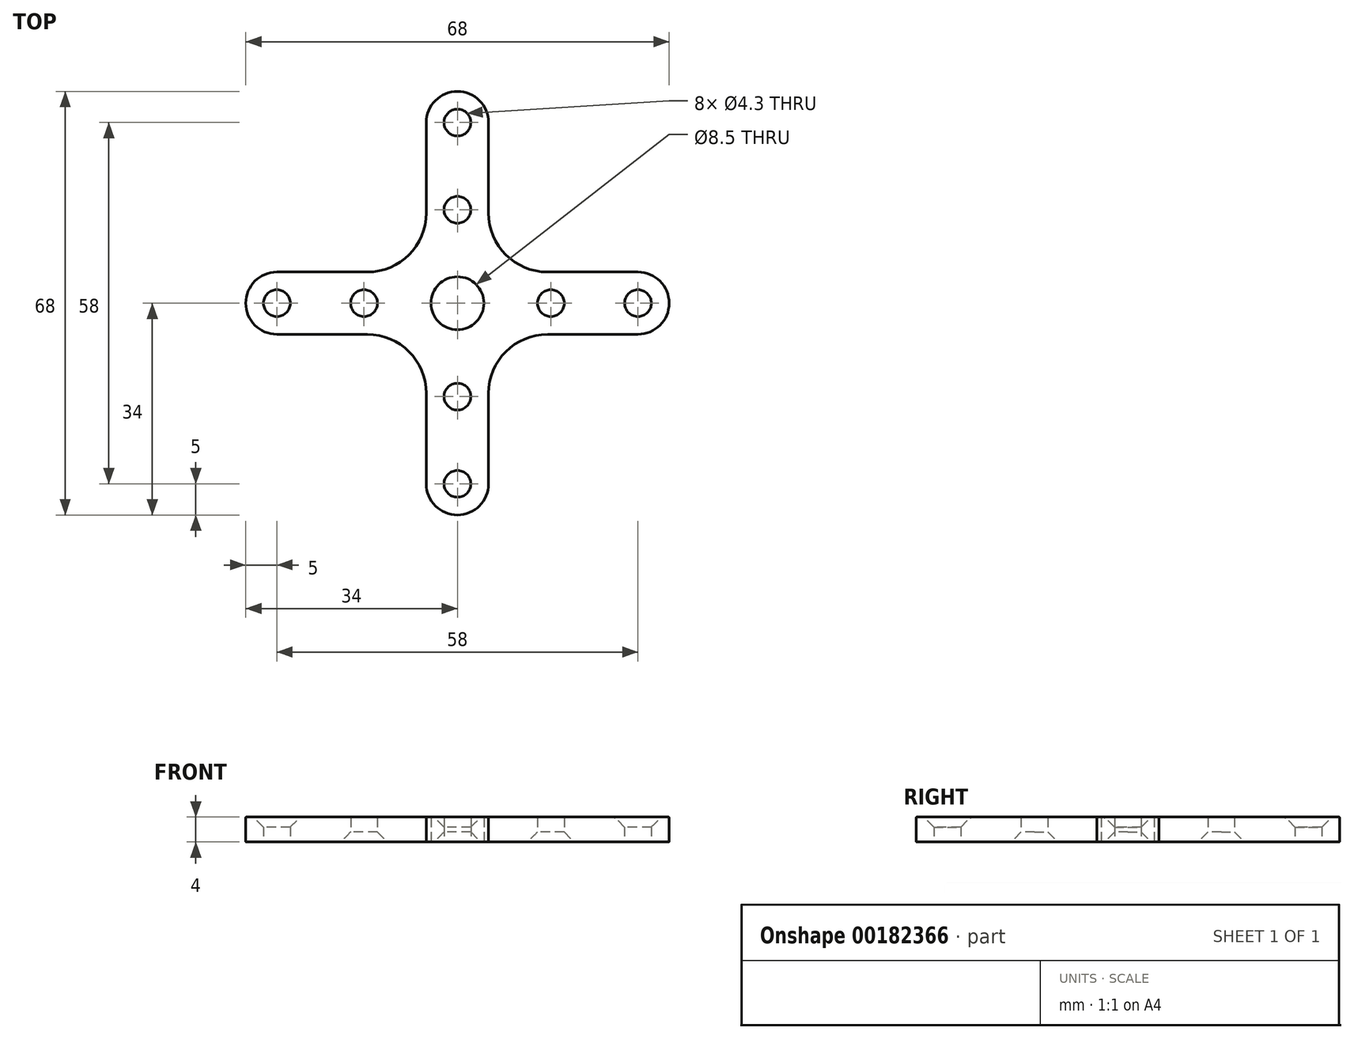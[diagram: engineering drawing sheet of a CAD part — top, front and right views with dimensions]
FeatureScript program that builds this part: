
annotation { "Feature Type Name" : "Feature", "Feature Type Description" : "" }
export const myFeature = defineFeature(function(context is Context, id is Id, definition is map)
    precondition{}
    {
        {
            var Q0;
            Q0=qCreatedBy(makeId("Top.planeOp"),FACE);
            var sketch = newSketch(context, id + "F0", { "sketchPlane" : qUnion([Q0])});
            skCircle(sketch, "E0", {"center": v(0, 0) * mm, "radius": 34 * mm, "construction": true});
            skCircle(sketch, "E1", {"center": v(0, 0) * mm, "radius": 29 * mm, "construction": true});
            skLineSegment(sketch, "E2", {"start": v(0, -42.55) * mm, "end": v(0, 44.51) * mm, "construction": true});
            skLineSegment(sketch, "E3", {"start": v(-47.28, 0) * mm, "end": v(50.22, 0) * mm, "construction": true});
            skCircle(sketch, "E4", {"center": v(0, 0) * mm, "radius": 11 * mm, "construction": true});
            skArc(sketch, "E5", {"start": v(5, 29) * mm, "mid": v(0, 34) * mm, "end": v(-5, 29) * mm});
            skArc(sketch, "E6", {"start": v(-29, 5) * mm, "mid": v(-34, 0) * mm, "end": v(-29, -5) * mm});
            skArc(sketch, "E7", {"start": v(29, -5) * mm, "mid": v(34, 0) * mm, "end": v(29, 5) * mm});
            skArc(sketch, "E8", {"start": v(-5, -29) * mm, "mid": v(0, -34) * mm, "end": v(5, -29) * mm});
            skArc(sketch, "E9", {"start": v(14.49, -5) * mm, "mid": v(7.78, -7.78) * mm, "end": v(5, -14.49) * mm});
            skArc(sketch, "E10", {"start": v(5, 14.49) * mm, "mid": v(7.78, 7.78) * mm, "end": v(14.49, 5) * mm});
            skArc(sketch, "E11", {"start": v(-14.49, 5) * mm, "mid": v(-7.78, 7.78) * mm, "end": v(-5, 14.49) * mm});
            skArc(sketch, "E12", {"start": v(-5, -14.49) * mm, "mid": v(-7.78, -7.78) * mm, "end": v(-14.49, -5) * mm});
            skCircle(sketch, "E13", {"center": v(0, 29) * mm, "radius": 2.15 * mm});
            skCircle(sketch, "E14", {"center": v(29, 0) * mm, "radius": 2.15 * mm});
            skCircle(sketch, "E15", {"center": v(0, -29) * mm, "radius": 2.15 * mm});
            skCircle(sketch, "E16", {"center": v(-29, 0) * mm, "radius": 2.15 * mm});
            skLineSegment(sketch, "E17.trimOffspring", {"start": v(-5, 14.49) * mm, "end": v(-5, 29) * mm});
            skLineSegment(sketch, "E18.trimOffspring", {"start": v(5, 14.49) * mm, "end": v(5, 29) * mm});
            skLineSegment(sketch, "E19.trimOffspring", {"start": v(14.49, 5) * mm, "end": v(29, 5) * mm});
            skLineSegment(sketch, "E20.trimOffspring", {"start": v(14.49, -5) * mm, "end": v(29, -5) * mm});
            skLineSegment(sketch, "E21.trimOffspring", {"start": v(-29, 5) * mm, "end": v(-14.49, 5) * mm});
            skLineSegment(sketch, "E22.trimOffspring", {"start": v(-29, -5) * mm, "end": v(-14.49, -5) * mm});
            skLineSegment(sketch, "E23.trimOffspring", {"start": v(-5, -29) * mm, "end": v(-5, -14.49) * mm});
            skLineSegment(sketch, "E24.trimOffspring", {"start": v(5, -29) * mm, "end": v(5, -14.49) * mm});
            skCircle(sketch, "E25", {"center": v(0, 0) * mm, "radius": 4.25 * mm});
            skCircle(sketch, "E26", {"center": v(0, 0) * mm, "radius": 15 * mm, "construction": true});
            skCircle(sketch, "E27", {"center": v(0, 15) * mm, "radius": 2.15 * mm});
            skCircle(sketch, "E28", {"center": v(-15, 0) * mm, "radius": 2.15 * mm});
            skCircle(sketch, "E29", {"center": v(0, -15) * mm, "radius": 2.15 * mm});
            skCircle(sketch, "E30", {"center": v(15, 0) * mm, "radius": 2.15 * mm});
            skSolve(sketch);
        }
        {
            var Q0;
            Q0 = qSketchRegion(id + "F0", true);
            extrude(context, id + "F1", {"entities" : qUnion([Q0]), "depth" : 4 * mm});
        }
        {
            var Q0;
            Q0=makeQuery(id+"F1.opExtrude","CAP_EDGE",EDGE,{"disambiguationData":[OSD([sQuery(id+"F0.wireOp",EDGE,"E13")])],"isStart":false});
            var Q1;
            Q1=makeQuery(id+"F1.opExtrude","CAP_EDGE",EDGE,{"disambiguationData":[OSD([sQuery(id+"F0.wireOp",EDGE,"E14")])],"isStart":false});
            var Q2;
            Q2=makeQuery(id+"F1.opExtrude","CAP_EDGE",EDGE,{"disambiguationData":[OSD([sQuery(id+"F0.wireOp",EDGE,"E15")])],"isStart":false});
            var Q3;
            Q3=makeQuery(id+"F1.opExtrude","CAP_EDGE",EDGE,{"disambiguationData":[OSD([sQuery(id+"F0.wireOp",EDGE,"E16")])],"isStart":false});
            chamfer(context, id + "F2", {"entities" : qUnion([Q0, Q1, Q2, Q3]), "width" : 1.6 * mm, "tangentPropagation" : true});
        }
        {
            var Q0;
            Q0=makeQuery(id+"F1.opExtrude","CAP_EDGE",EDGE,{"disambiguationData":[OSD([sQuery(id+"F0.wireOp",EDGE,"E29")])],"isStart":true});
            var Q1;
            Q1=makeQuery(id+"F1.opExtrude","CAP_EDGE",EDGE,{"disambiguationData":[OSD([sQuery(id+"F0.wireOp",EDGE,"E28")])],"isStart":true});
            var Q2;
            Q2=makeQuery(id+"F1.opExtrude","CAP_EDGE",EDGE,{"disambiguationData":[OSD([sQuery(id+"F0.wireOp",EDGE,"E27")])],"isStart":true});
            var Q3;
            Q3=makeQuery(id+"F1.opExtrude","CAP_EDGE",EDGE,{"disambiguationData":[OSD([sQuery(id+"F0.wireOp",EDGE,"E30")])],"isStart":true});
            chamfer(context, id + "F3", {"entities" : qUnion([Q0, Q1, Q2, Q3]), "width" : 1.6 * mm, "tangentPropagation" : true});
        }
        {
            var Q0;
            Q0=makeQuery(id+"F1.opExtrude","CAP_FACE",FACE,{"disambiguationData":[OSD([sQuery(id+"F0.wireOp",EDGE,"E5"),sQuery(id+"F0.wireOp",EDGE,"E6"),sQuery(id+"F0.wireOp",EDGE,"E7"),sQuery(id+"F0.wireOp",EDGE,"E8"),sQuery(id+"F0.wireOp",EDGE,"E9"),sQuery(id+"F0.wireOp",EDGE,"E10"),sQuery(id+"F0.wireOp",EDGE,"E11"),sQuery(id+"F0.wireOp",EDGE,"E12"),sQuery(id+"F0.wireOp",EDGE,"E13"),sQuery(id+"F0.wireOp",EDGE,"E14"),sQuery(id+"F0.wireOp",EDGE,"E15"),sQuery(id+"F0.wireOp",EDGE,"E16"),sQuery(id+"F0.wireOp",EDGE,"E17.trimOffspring"),sQuery(id+"F0.wireOp",EDGE,"E18.trimOffspring"),sQuery(id+"F0.wireOp",EDGE,"E19.trimOffspring"),sQuery(id+"F0.wireOp",EDGE,"E20.trimOffspring"),sQuery(id+"F0.wireOp",EDGE,"E21.trimOffspring"),sQuery(id+"F0.wireOp",EDGE,"E22.trimOffspring"),sQuery(id+"F0.wireOp",EDGE,"E23.trimOffspring"),sQuery(id+"F0.wireOp",EDGE,"E24.trimOffspring"),sQuery(id+"F0.wireOp",EDGE,"E25"),sQuery(id+"F0.wireOp",EDGE,"E27"),sQuery(id+"F0.wireOp",EDGE,"E28"),sQuery(id+"F0.wireOp",EDGE,"E29"),sQuery(id+"F0.wireOp",EDGE,"E30")])],"isStart":false});
            fillet(context, id + "F4", {"entities" : qUnion([Q0]), "radius" : 0.1 * mm, "tangentPropagation" : true, "allowEdgeOverflow" : false});
        }
        {
            var Q0;
            Q0=makeQuery(id+"F1.opExtrude","CAP_FACE",FACE,{"disambiguationData":[OSD([sQuery(id+"F0.wireOp",EDGE,"E5"),sQuery(id+"F0.wireOp",EDGE,"E6"),sQuery(id+"F0.wireOp",EDGE,"E7"),sQuery(id+"F0.wireOp",EDGE,"E8"),sQuery(id+"F0.wireOp",EDGE,"E9"),sQuery(id+"F0.wireOp",EDGE,"E10"),sQuery(id+"F0.wireOp",EDGE,"E11"),sQuery(id+"F0.wireOp",EDGE,"E12"),sQuery(id+"F0.wireOp",EDGE,"E13"),sQuery(id+"F0.wireOp",EDGE,"E14"),sQuery(id+"F0.wireOp",EDGE,"E15"),sQuery(id+"F0.wireOp",EDGE,"E16"),sQuery(id+"F0.wireOp",EDGE,"E17.trimOffspring"),sQuery(id+"F0.wireOp",EDGE,"E18.trimOffspring"),sQuery(id+"F0.wireOp",EDGE,"E19.trimOffspring"),sQuery(id+"F0.wireOp",EDGE,"E20.trimOffspring"),sQuery(id+"F0.wireOp",EDGE,"E21.trimOffspring"),sQuery(id+"F0.wireOp",EDGE,"E22.trimOffspring"),sQuery(id+"F0.wireOp",EDGE,"E23.trimOffspring"),sQuery(id+"F0.wireOp",EDGE,"E24.trimOffspring"),sQuery(id+"F0.wireOp",EDGE,"E25"),sQuery(id+"F0.wireOp",EDGE,"E27"),sQuery(id+"F0.wireOp",EDGE,"E28"),sQuery(id+"F0.wireOp",EDGE,"E29"),sQuery(id+"F0.wireOp",EDGE,"E30")])],"isStart":true});
            fillet(context, id + "F5", {"entities" : qUnion([Q0]), "radius" : 0.1 * mm, "tangentPropagation" : true, "allowEdgeOverflow" : false});
        }
    });
